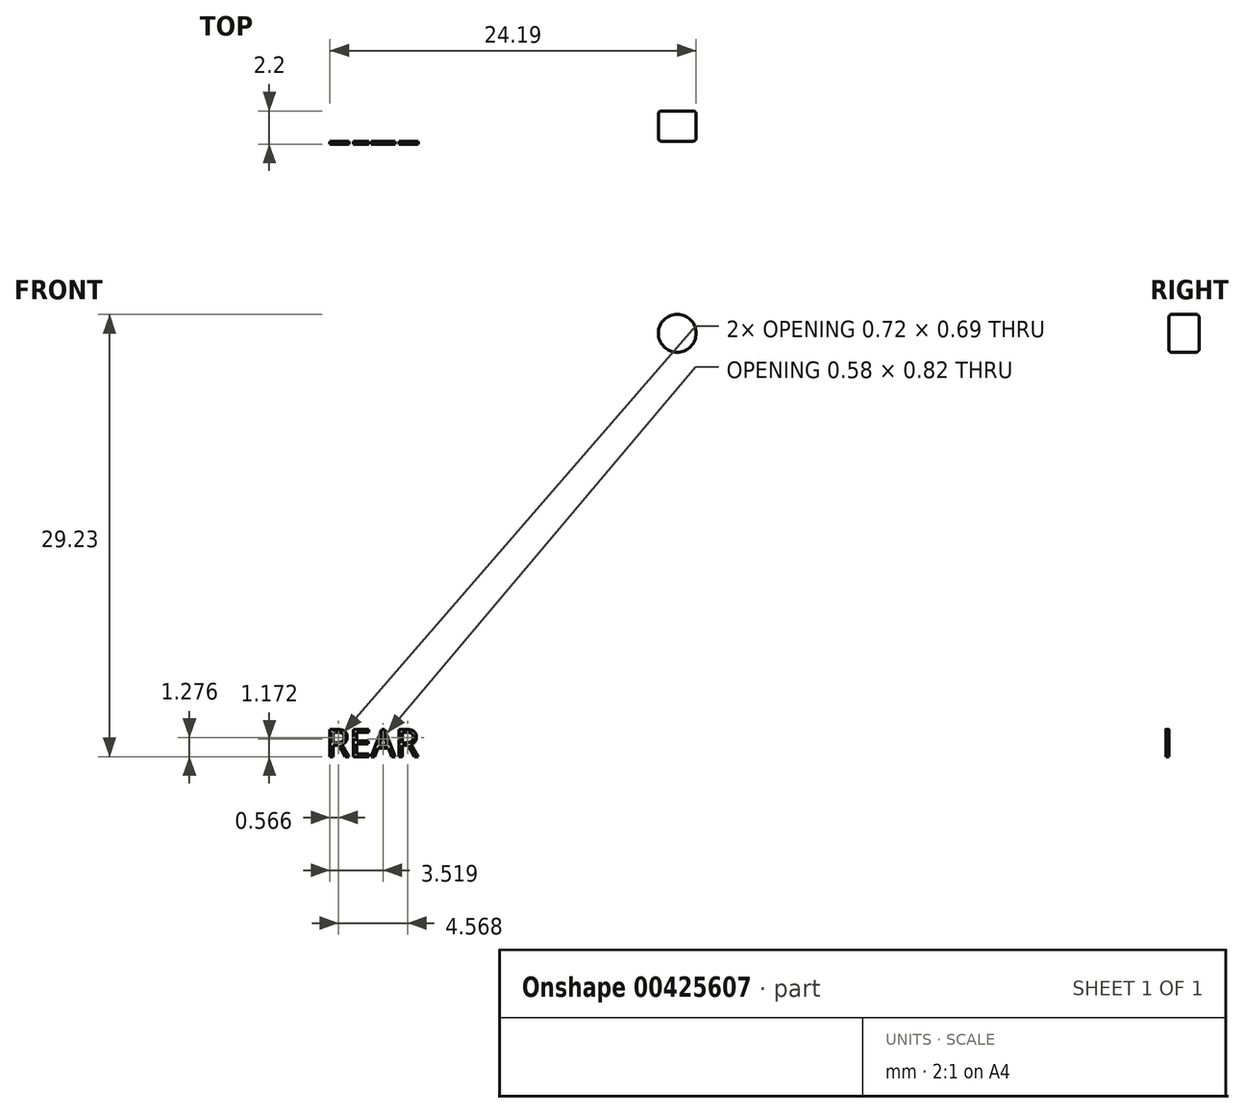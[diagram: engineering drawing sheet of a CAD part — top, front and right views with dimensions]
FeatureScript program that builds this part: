
annotation { "Feature Type Name" : "Feature", "Feature Type Description" : "" }
export const myFeature = defineFeature(function(context is Context, id is Id, definition is map)
    precondition{}
    {
        {
            var Q0;
            Q0=qCreatedBy(makeId("Front.planeOp"),FACE);
            var sketch = newSketch(context, id + "F0", { "sketchPlane" : qUnion([Q0])});
            skCircle(sketch, "E0", {"center": v(20.14, 10.68) * mm, "radius": 1.25 * mm});
            skCircle(sketch, "E1", {"center": v(20.14, -7.32) * mm, "radius": 1.25 * mm});
            skCircle(sketch, "E2", {"center": v(-19.86, 10.68) * mm, "radius": 1.25 * mm});
            skCircle(sketch, "E3", {"center": v(-19.86, -7.32) * mm, "radius": 1.25 * mm});
            skLineSegment(sketch, "E4", {"start": v(-13.86, 19.68) * mm, "end": v(14.15, 19.68) * mm});
            skLineSegment(sketch, "E5", {"start": v(-23.1, 11.7) * mm, "end": v(-23.1, -6.69) * mm});
            skLineSegment(sketch, "E6", {"start": v(23.4, 11.94) * mm, "end": v(23.4, -6.69) * mm});
            skLineSegment(sketch, "E7", {"start": v(14, -19.32) * mm, "end": v(-13.7, -19.32) * mm});
            skLineSegment(sketch, "E8", {"start": v(-23.1, 11.7) * mm, "end": v(-23.1, 11.94) * mm});
            skLineSegment(sketch, "E9", {"start": v(-22.5, 13.75) * mm, "end": v(-16.26, 18.5) * mm});
            skLineSegment(sketch, "E10", {"start": v(-22.64, -8.3) * mm, "end": v(-16.24, -17.92) * mm});
            skLineSegment(sketch, "E11", {"start": v(16.53, -17.92) * mm, "end": v(22.93, -8.3) * mm});
            skLineSegment(sketch, "E12", {"start": v(22.79, 13.75) * mm, "end": v(16.54, 18.5) * mm});
            skArc(sketch, "E13", {"start": v(-16.26, 18.5) * mm, "mid": v(-15.2, 19.37) * mm, "end": v(-13.86, 19.68) * mm});
            skArc(sketch, "E14", {"start": v(16.54, 18.5) * mm, "mid": v(15.49, 19.37) * mm, "end": v(14.15, 19.68) * mm});
            skArc(sketch, "E15", {"start": v(22.79, 13.75) * mm, "mid": v(23.24, 12.9) * mm, "end": v(23.4, 11.94) * mm});
            skArc(sketch, "E16", {"start": v(23.4, -6.69) * mm, "mid": v(23.28, -7.52) * mm, "end": v(22.93, -8.3) * mm});
            skArc(sketch, "E17", {"start": v(16.53, -17.92) * mm, "mid": v(15.44, -18.94) * mm, "end": v(14, -19.32) * mm});
            skArc(sketch, "E18", {"start": v(-13.7, -19.32) * mm, "mid": v(-15.15, -18.94) * mm, "end": v(-16.24, -17.92) * mm});
            skArc(sketch, "E19", {"start": v(-22.64, -8.3) * mm, "mid": v(-22.99, -7.52) * mm, "end": v(-23.1, -6.69) * mm});
            skArc(sketch, "E20", {"start": v(-23.1, 11.94) * mm, "mid": v(-22.95, 12.9) * mm, "end": v(-22.5, 13.75) * mm});
            skLineSegment(sketch, "E21", {"start": v(-15.36, -13.32) * mm, "end": v(-15.36, -16.32) * mm});
            skLineSegment(sketch, "E22", {"start": v(-12.36, -16.32) * mm, "end": v(-12.36, -13.32) * mm});
            skArc(sketch, "E23", {"start": v(-15.36, -16.32) * mm, "mid": v(-13.86, -17.82) * mm, "end": v(-12.36, -16.32) * mm});
            skArc(sketch, "E24", {"start": v(-12.36, -13.32) * mm, "mid": v(-13.86, -11.82) * mm, "end": v(-15.36, -13.32) * mm});
            skLineSegment(sketch, "E25", {"start": v(-15.36, 16.68) * mm, "end": v(-15.36, 13.68) * mm});
            skLineSegment(sketch, "E26", {"start": v(-12.36, 13.68) * mm, "end": v(-12.36, 16.68) * mm});
            skArc(sketch, "E27", {"start": v(-15.36, 13.68) * mm, "mid": v(-13.86, 12.18) * mm, "end": v(-12.36, 13.68) * mm});
            skArc(sketch, "E28", {"start": v(-12.36, 16.68) * mm, "mid": v(-13.86, 18.18) * mm, "end": v(-15.36, 16.68) * mm});
            skLineSegment(sketch, "E29", {"start": v(12.64, 16.68) * mm, "end": v(12.64, 13.68) * mm});
            skLineSegment(sketch, "E30", {"start": v(15.64, 13.68) * mm, "end": v(15.64, 16.68) * mm});
            skArc(sketch, "E31", {"start": v(12.64, 13.68) * mm, "mid": v(14.14, 12.18) * mm, "end": v(15.64, 13.68) * mm});
            skArc(sketch, "E32", {"start": v(15.64, 16.68) * mm, "mid": v(14.14, 18.18) * mm, "end": v(12.64, 16.68) * mm});
            skLineSegment(sketch, "E33", {"start": v(12.64, -13.32) * mm, "end": v(12.64, -16.32) * mm});
            skLineSegment(sketch, "E34", {"start": v(15.64, -16.32) * mm, "end": v(15.64, -13.32) * mm});
            skArc(sketch, "E35", {"start": v(12.64, -16.32) * mm, "mid": v(14.14, -17.82) * mm, "end": v(15.64, -16.32) * mm});
            skArc(sketch, "E36", {"start": v(15.64, -13.32) * mm, "mid": v(14.14, -11.82) * mm, "end": v(12.64, -13.32) * mm});
            skLineSegment(sketch, "E37", {"start": v(-9.86, 7.68) * mm, "end": v(-9.86, -7.32) * mm});
            skLineSegment(sketch, "E38", {"start": v(-6.86, -10.32) * mm, "end": v(7.14, -10.32) * mm});
            skLineSegment(sketch, "E39", {"start": v(10.14, -7.32) * mm, "end": v(10.14, 7.68) * mm});
            skLineSegment(sketch, "E40", {"start": v(7.14, 10.68) * mm, "end": v(-6.86, 10.68) * mm});
            skLineSegment(sketch, "E41", {"start": v(0.14, 19.68) * mm, "end": v(1.97, 19.68) * mm});
            skArc(sketch, "E42.filletArc", {"start": v(-6.86, 10.68) * mm, "mid": v(-8.98, 9.8) * mm, "end": v(-9.86, 7.68) * mm});
            skArc(sketch, "E43.filletArc", {"start": v(10.14, 7.68) * mm, "mid": v(9.26, 9.8) * mm, "end": v(7.14, 10.68) * mm});
            skArc(sketch, "E44.filletArc", {"start": v(7.14, -10.32) * mm, "mid": v(9.26, -9.44) * mm, "end": v(10.14, -7.32) * mm});
            skArc(sketch, "E45.filletArc", {"start": v(-9.86, -7.32) * mm, "mid": v(-8.98, -9.44) * mm, "end": v(-6.86, -10.32) * mm});
            skSolve(sketch);
        }
        {
            var Q0;
            Q0=makeQuery(id+"F0.imprint","IMPRINT",FACE,{"disambiguationData":[TD([[makeQuery(id+"F0.imprint","IMPRINT",EDGE,{"derivedFrom":sQuery(id+"F0.wireOp",EDGE,"E0")}),1.0]])]});
            extrude(context, id + "F1", {"entities" : qUnion([Q0]), "endBound" : BoundingType.SYMMETRIC, "depth" : 2 * mm});
        }
        {
            var Q0;
            Q0=makeQuery(id+"F1.opExtrude","CAP_FACE",FACE,{"disambiguationData":[OSD([sQuery(id+"F0.wireOp",EDGE,"b1f0e1de-7193-468a-b55f-a6da741b84d3"),sQuery(id+"F0.wireOp",EDGE,"6537f49a-e45f-4989-940a-a7038c38fff4"),sQuery(id+"F0.wireOp",EDGE,"8788dc07-e2e4-47d1-917b-d93742f93994"),sQuery(id+"F0.wireOp",EDGE,"47e42d19-3951-40ac-b4fd-01fcafdaa09f"),sQuery(id+"F0.wireOp",EDGE,"50e5991a-f910-4297-a0f5-58b0cc2bc1d4"),sQuery(id+"F0.wireOp",EDGE,"833c6bdf-bbd0-4c9a-a248-ca72598f08ba"),sQuery(id+"F0.wireOp",EDGE,"bd7a1b35-b3c5-4d82-882c-69e7568a474c"),sQuery(id+"F0.wireOp",EDGE,"ed142891-9665-4ff3-9cbf-df6a8f694267"),sQuery(id+"F0.wireOp",EDGE,"23a40c6b-513f-4e2b-90a4-2960991b2cb5"),sQuery(id+"F0.wireOp",EDGE,"b176ce0e-36f0-4206-846a-287cc205a3f0"),sQuery(id+"F0.wireOp",EDGE,"fd2f453c-b56c-4dc5-826e-d680bcd9d531"),sQuery(id+"F0.wireOp",EDGE,"4c904b9e-ebe1-46e0-9133-f6789165a817"),sQuery(id+"F0.wireOp",EDGE,"7d301a29-2a78-4614-95a1-4e57b7e65221"),sQuery(id+"F0.wireOp",EDGE,"bb945b4e-dbfa-4606-a6d0-c193b2a083f5"),sQuery(id+"F0.wireOp",EDGE,"f4a1adec-4f2b-4cc0-960b-66cac54fa532"),sQuery(id+"F0.wireOp",EDGE,"62c7bd33-5918-4929-8abe-04f5cd03c51a"),sQuery(id+"F0.wireOp",EDGE,"ff2f2cbf-8293-4aa6-ab80-3f50b4d68cad"),sQuery(id+"F0.wireOp",EDGE,"c173fb08-37eb-45d5-abb3-169ab915dbf1"),sQuery(id+"F0.wireOp",EDGE,"3b8e2cb5-3b84-4c06-aae3-f4915deb625e"),sQuery(id+"F0.wireOp",EDGE,"4d7a7edb-dbb5-48c5-942c-85668880a151"),sQuery(id+"F0.wireOp",EDGE,"bc3c386a-a424-47c6-a6fb-62494ecd1ae2"),sQuery(id+"F0.wireOp",EDGE,"e67013cf-1ebe-4a99-9c97-0e6cbc980e63"),sQuery(id+"F0.wireOp",EDGE,"a818867e-71c0-43a4-8c8c-aa08c8f7215a"),sQuery(id+"F0.wireOp",EDGE,"b38f441d-59fa-4f63-924d-4ace32872c36"),sQuery(id+"F0.wireOp",EDGE,"816ea5cf-f9e5-4ce4-9dad-646165a54645"),sQuery(id+"F0.wireOp",EDGE,"facd8c0d-b804-4209-a28e-61043daaaeb2"),sQuery(id+"F0.wireOp",EDGE,"7b894aa8-54af-4764-99a5-ba58160ee854"),sQuery(id+"F0.wireOp",EDGE,"c65d9a3e-1ebe-4f95-b916-c5048aa1f32a"),sQuery(id+"F0.wireOp",EDGE,"8a8d933c-0f1d-4399-bc31-42f5874e0fa8"),sQuery(id+"F0.wireOp",EDGE,"5d736322-692b-4da4-8669-e5a22c50adb5"),sQuery(id+"F0.wireOp",EDGE,"abe0f840-d98d-4ca2-984c-8d9502a8e020"),sQuery(id+"F0.wireOp",EDGE,"c0335e12-add7-4a7a-9bef-f67fba7cfbac"),sQuery(id+"F0.wireOp",EDGE,"2affc33d-ac1f-4258-a0ef-0d6ff35947cf"),sQuery(id+"F0.wireOp",EDGE,"5b7d1504-a426-47d7-bc96-b206599dc827"),sQuery(id+"F0.wireOp",EDGE,"a08130f0-2d8c-49ea-a9e2-bc1175a15415"),sQuery(id+"F0.wireOp",EDGE,"5b375d67-10b6-40a0-8c18-0bca81d9af6a"),sQuery(id+"F0.wireOp",EDGE,"d0d2f69b-842c-4d9c-a6f7-bc08b85c3292")])],"isStart":false});
            var Q1;
            Q1=makeQuery(id+"F1.opExtrude","CAP_FACE",FACE,{"disambiguationData":[OSD([sQuery(id+"F0.wireOp",EDGE,"b1f0e1de-7193-468a-b55f-a6da741b84d3"),sQuery(id+"F0.wireOp",EDGE,"6537f49a-e45f-4989-940a-a7038c38fff4"),sQuery(id+"F0.wireOp",EDGE,"8788dc07-e2e4-47d1-917b-d93742f93994"),sQuery(id+"F0.wireOp",EDGE,"47e42d19-3951-40ac-b4fd-01fcafdaa09f"),sQuery(id+"F0.wireOp",EDGE,"50e5991a-f910-4297-a0f5-58b0cc2bc1d4"),sQuery(id+"F0.wireOp",EDGE,"833c6bdf-bbd0-4c9a-a248-ca72598f08ba"),sQuery(id+"F0.wireOp",EDGE,"bd7a1b35-b3c5-4d82-882c-69e7568a474c"),sQuery(id+"F0.wireOp",EDGE,"ed142891-9665-4ff3-9cbf-df6a8f694267"),sQuery(id+"F0.wireOp",EDGE,"23a40c6b-513f-4e2b-90a4-2960991b2cb5"),sQuery(id+"F0.wireOp",EDGE,"b176ce0e-36f0-4206-846a-287cc205a3f0"),sQuery(id+"F0.wireOp",EDGE,"fd2f453c-b56c-4dc5-826e-d680bcd9d531"),sQuery(id+"F0.wireOp",EDGE,"4c904b9e-ebe1-46e0-9133-f6789165a817"),sQuery(id+"F0.wireOp",EDGE,"7d301a29-2a78-4614-95a1-4e57b7e65221"),sQuery(id+"F0.wireOp",EDGE,"bb945b4e-dbfa-4606-a6d0-c193b2a083f5"),sQuery(id+"F0.wireOp",EDGE,"f4a1adec-4f2b-4cc0-960b-66cac54fa532"),sQuery(id+"F0.wireOp",EDGE,"62c7bd33-5918-4929-8abe-04f5cd03c51a"),sQuery(id+"F0.wireOp",EDGE,"ff2f2cbf-8293-4aa6-ab80-3f50b4d68cad"),sQuery(id+"F0.wireOp",EDGE,"c173fb08-37eb-45d5-abb3-169ab915dbf1"),sQuery(id+"F0.wireOp",EDGE,"3b8e2cb5-3b84-4c06-aae3-f4915deb625e"),sQuery(id+"F0.wireOp",EDGE,"4d7a7edb-dbb5-48c5-942c-85668880a151"),sQuery(id+"F0.wireOp",EDGE,"bc3c386a-a424-47c6-a6fb-62494ecd1ae2"),sQuery(id+"F0.wireOp",EDGE,"e67013cf-1ebe-4a99-9c97-0e6cbc980e63"),sQuery(id+"F0.wireOp",EDGE,"a818867e-71c0-43a4-8c8c-aa08c8f7215a"),sQuery(id+"F0.wireOp",EDGE,"b38f441d-59fa-4f63-924d-4ace32872c36"),sQuery(id+"F0.wireOp",EDGE,"816ea5cf-f9e5-4ce4-9dad-646165a54645"),sQuery(id+"F0.wireOp",EDGE,"facd8c0d-b804-4209-a28e-61043daaaeb2"),sQuery(id+"F0.wireOp",EDGE,"7b894aa8-54af-4764-99a5-ba58160ee854"),sQuery(id+"F0.wireOp",EDGE,"c65d9a3e-1ebe-4f95-b916-c5048aa1f32a"),sQuery(id+"F0.wireOp",EDGE,"8a8d933c-0f1d-4399-bc31-42f5874e0fa8"),sQuery(id+"F0.wireOp",EDGE,"5d736322-692b-4da4-8669-e5a22c50adb5"),sQuery(id+"F0.wireOp",EDGE,"abe0f840-d98d-4ca2-984c-8d9502a8e020"),sQuery(id+"F0.wireOp",EDGE,"c0335e12-add7-4a7a-9bef-f67fba7cfbac"),sQuery(id+"F0.wireOp",EDGE,"2affc33d-ac1f-4258-a0ef-0d6ff35947cf"),sQuery(id+"F0.wireOp",EDGE,"5b7d1504-a426-47d7-bc96-b206599dc827"),sQuery(id+"F0.wireOp",EDGE,"a08130f0-2d8c-49ea-a9e2-bc1175a15415"),sQuery(id+"F0.wireOp",EDGE,"5b375d67-10b6-40a0-8c18-0bca81d9af6a"),sQuery(id+"F0.wireOp",EDGE,"d0d2f69b-842c-4d9c-a6f7-bc08b85c3292")])],"isStart":true});
            var Q2;
            Q2=makeQuery(id+"F1.opExtrude","CAP_FACE",FACE,{"disambiguationData":[OSD([sQuery(id+"F0.wireOp",EDGE,"E0"),sQuery(id+"F0.wireOp",EDGE,"E1"),sQuery(id+"F0.wireOp",EDGE,"E2"),sQuery(id+"F0.wireOp",EDGE,"E3"),sQuery(id+"F0.wireOp",EDGE,"E4"),sQuery(id+"F0.wireOp",EDGE,"E5"),sQuery(id+"F0.wireOp",EDGE,"E6"),sQuery(id+"F0.wireOp",EDGE,"E7"),sQuery(id+"F0.wireOp",EDGE,"E8"),sQuery(id+"F0.wireOp",EDGE,"E9"),sQuery(id+"F0.wireOp",EDGE,"E10"),sQuery(id+"F0.wireOp",EDGE,"E11"),sQuery(id+"F0.wireOp",EDGE,"E12"),sQuery(id+"F0.wireOp",EDGE,"E13"),sQuery(id+"F0.wireOp",EDGE,"E14"),sQuery(id+"F0.wireOp",EDGE,"E15"),sQuery(id+"F0.wireOp",EDGE,"E16"),sQuery(id+"F0.wireOp",EDGE,"E17"),sQuery(id+"F0.wireOp",EDGE,"E18"),sQuery(id+"F0.wireOp",EDGE,"E19"),sQuery(id+"F0.wireOp",EDGE,"E20"),sQuery(id+"F0.wireOp",EDGE,"E21"),sQuery(id+"F0.wireOp",EDGE,"E22"),sQuery(id+"F0.wireOp",EDGE,"E23"),sQuery(id+"F0.wireOp",EDGE,"E24"),sQuery(id+"F0.wireOp",EDGE,"E25"),sQuery(id+"F0.wireOp",EDGE,"E26"),sQuery(id+"F0.wireOp",EDGE,"E27"),sQuery(id+"F0.wireOp",EDGE,"E28"),sQuery(id+"F0.wireOp",EDGE,"E29"),sQuery(id+"F0.wireOp",EDGE,"E30"),sQuery(id+"F0.wireOp",EDGE,"E31"),sQuery(id+"F0.wireOp",EDGE,"E32"),sQuery(id+"F0.wireOp",EDGE,"E33"),sQuery(id+"F0.wireOp",EDGE,"E34"),sQuery(id+"F0.wireOp",EDGE,"E35"),sQuery(id+"F0.wireOp",EDGE,"E36"),sQuery(id+"F0.wireOp",EDGE,"E37"),sQuery(id+"F0.wireOp",EDGE,"E38"),sQuery(id+"F0.wireOp",EDGE,"E39"),sQuery(id+"F0.wireOp",EDGE,"E40"),sQuery(id+"F0.wireOp",EDGE,"E41"),sQuery(id+"F0.wireOp",EDGE,"23430ce5-24f0-485a-982d-6951f8ba1cb3"),sQuery(id+"F0.wireOp",EDGE,"e361aa3b-1d09-4de2-9852-f016a7084046"),sQuery(id+"F0.wireOp",EDGE,"3cd874c0-05b7-48c2-b5ff-4c1055a05f93"),sQuery(id+"F0.wireOp",EDGE,"ebd2ca65-28b3-4523-afe8-6085c673d042")])],"isStart":false});
            fillet(context, id + "F2", {"entities" : qUnion([Q0, Q1, Q2]), "radius" : .2 * mm, "tangentPropagation" : true, "allowEdgeOverflow" : false});
        }
        {
            var Q0;
            Q0=makeQuery(id+"F1.opExtrude","CAP_FACE",FACE,{"disambiguationData":[OSD([sQuery(id+"F0.wireOp",EDGE,"E0"),sQuery(id+"F0.wireOp",EDGE,"E1"),sQuery(id+"F0.wireOp",EDGE,"E2"),sQuery(id+"F0.wireOp",EDGE,"E3"),sQuery(id+"F0.wireOp",EDGE,"E4"),sQuery(id+"F0.wireOp",EDGE,"E5"),sQuery(id+"F0.wireOp",EDGE,"E6"),sQuery(id+"F0.wireOp",EDGE,"E7"),sQuery(id+"F0.wireOp",EDGE,"E8"),sQuery(id+"F0.wireOp",EDGE,"E9"),sQuery(id+"F0.wireOp",EDGE,"E10"),sQuery(id+"F0.wireOp",EDGE,"E11"),sQuery(id+"F0.wireOp",EDGE,"E12"),sQuery(id+"F0.wireOp",EDGE,"E13"),sQuery(id+"F0.wireOp",EDGE,"E14"),sQuery(id+"F0.wireOp",EDGE,"E15"),sQuery(id+"F0.wireOp",EDGE,"E16"),sQuery(id+"F0.wireOp",EDGE,"E17"),sQuery(id+"F0.wireOp",EDGE,"E18"),sQuery(id+"F0.wireOp",EDGE,"E19"),sQuery(id+"F0.wireOp",EDGE,"E20"),sQuery(id+"F0.wireOp",EDGE,"E21"),sQuery(id+"F0.wireOp",EDGE,"E22"),sQuery(id+"F0.wireOp",EDGE,"E23"),sQuery(id+"F0.wireOp",EDGE,"E24"),sQuery(id+"F0.wireOp",EDGE,"E25"),sQuery(id+"F0.wireOp",EDGE,"E26"),sQuery(id+"F0.wireOp",EDGE,"E27"),sQuery(id+"F0.wireOp",EDGE,"E28"),sQuery(id+"F0.wireOp",EDGE,"E29"),sQuery(id+"F0.wireOp",EDGE,"E30"),sQuery(id+"F0.wireOp",EDGE,"E31"),sQuery(id+"F0.wireOp",EDGE,"E32"),sQuery(id+"F0.wireOp",EDGE,"E33"),sQuery(id+"F0.wireOp",EDGE,"E34"),sQuery(id+"F0.wireOp",EDGE,"E35"),sQuery(id+"F0.wireOp",EDGE,"E36"),sQuery(id+"F0.wireOp",EDGE,"E37"),sQuery(id+"F0.wireOp",EDGE,"E38"),sQuery(id+"F0.wireOp",EDGE,"E39"),sQuery(id+"F0.wireOp",EDGE,"E40"),sQuery(id+"F0.wireOp",EDGE,"E41"),sQuery(id+"F0.wireOp",EDGE,"23430ce5-24f0-485a-982d-6951f8ba1cb3"),sQuery(id+"F0.wireOp",EDGE,"e361aa3b-1d09-4de2-9852-f016a7084046"),sQuery(id+"F0.wireOp",EDGE,"3cd874c0-05b7-48c2-b5ff-4c1055a05f93"),sQuery(id+"F0.wireOp",EDGE,"ebd2ca65-28b3-4523-afe8-6085c673d042")])],"isStart":true});
            fillet(context, id + "F3", {"entities" : qUnion([Q0]), "radius" : .2 * mm, "tangentPropagation" : true, "allowEdgeOverflow" : false});
        }
        {
            var Q0;
            Q0=makeQuery(id+"F1.opExtrude","CAP_FACE",FACE,{"disambiguationData":[OSD([sQuery(id+"F0.wireOp",EDGE,"E0"),sQuery(id+"F0.wireOp",EDGE,"E1"),sQuery(id+"F0.wireOp",EDGE,"E2"),sQuery(id+"F0.wireOp",EDGE,"E3"),sQuery(id+"F0.wireOp",EDGE,"E4"),sQuery(id+"F0.wireOp",EDGE,"E5"),sQuery(id+"F0.wireOp",EDGE,"E6"),sQuery(id+"F0.wireOp",EDGE,"E7"),sQuery(id+"F0.wireOp",EDGE,"E8"),sQuery(id+"F0.wireOp",EDGE,"E9"),sQuery(id+"F0.wireOp",EDGE,"E10"),sQuery(id+"F0.wireOp",EDGE,"E11"),sQuery(id+"F0.wireOp",EDGE,"E12"),sQuery(id+"F0.wireOp",EDGE,"E13"),sQuery(id+"F0.wireOp",EDGE,"E14"),sQuery(id+"F0.wireOp",EDGE,"E15"),sQuery(id+"F0.wireOp",EDGE,"E16"),sQuery(id+"F0.wireOp",EDGE,"E17"),sQuery(id+"F0.wireOp",EDGE,"E18"),sQuery(id+"F0.wireOp",EDGE,"E19"),sQuery(id+"F0.wireOp",EDGE,"E20"),sQuery(id+"F0.wireOp",EDGE,"E21"),sQuery(id+"F0.wireOp",EDGE,"E22"),sQuery(id+"F0.wireOp",EDGE,"E23"),sQuery(id+"F0.wireOp",EDGE,"E24"),sQuery(id+"F0.wireOp",EDGE,"E25"),sQuery(id+"F0.wireOp",EDGE,"E26"),sQuery(id+"F0.wireOp",EDGE,"E27"),sQuery(id+"F0.wireOp",EDGE,"E28"),sQuery(id+"F0.wireOp",EDGE,"E29"),sQuery(id+"F0.wireOp",EDGE,"E30"),sQuery(id+"F0.wireOp",EDGE,"E31"),sQuery(id+"F0.wireOp",EDGE,"E32"),sQuery(id+"F0.wireOp",EDGE,"E33"),sQuery(id+"F0.wireOp",EDGE,"E34"),sQuery(id+"F0.wireOp",EDGE,"E35"),sQuery(id+"F0.wireOp",EDGE,"E36"),sQuery(id+"F0.wireOp",EDGE,"E37"),sQuery(id+"F0.wireOp",EDGE,"E38"),sQuery(id+"F0.wireOp",EDGE,"E39"),sQuery(id+"F0.wireOp",EDGE,"E40"),sQuery(id+"F0.wireOp",EDGE,"E41"),sQuery(id+"F0.wireOp",EDGE,"E42.filletArc"),sQuery(id+"F0.wireOp",EDGE,"E43.filletArc"),sQuery(id+"F0.wireOp",EDGE,"E44.filletArc"),sQuery(id+"F0.wireOp",EDGE,"E45.filletArc")])],"isStart":false});
            var sketch = newSketch(context, id + "F4", { "sketchPlane" : qUnion([Q0])});
            skText(sketch, "E46", { "text": "REAR", "fontName": "OpenSans-Regular.ttf"});
            const initialGuessF4  = {"E46": [-0.00305, -0.0173, 1, 0, 0.00182]};
            skSetInitialGuess(sketch, initialGuessF4);
            skSolve(sketch);
        }
        {
            var Q0;
            Q0 = qSketchRegion(id + "F4", true);
            extrude(context, id + "F5", {"entities" : qUnion([Q0]), "operationType" : NewBodyOperationType.ADD, "depth" : .2 * mm});
        }
    });
